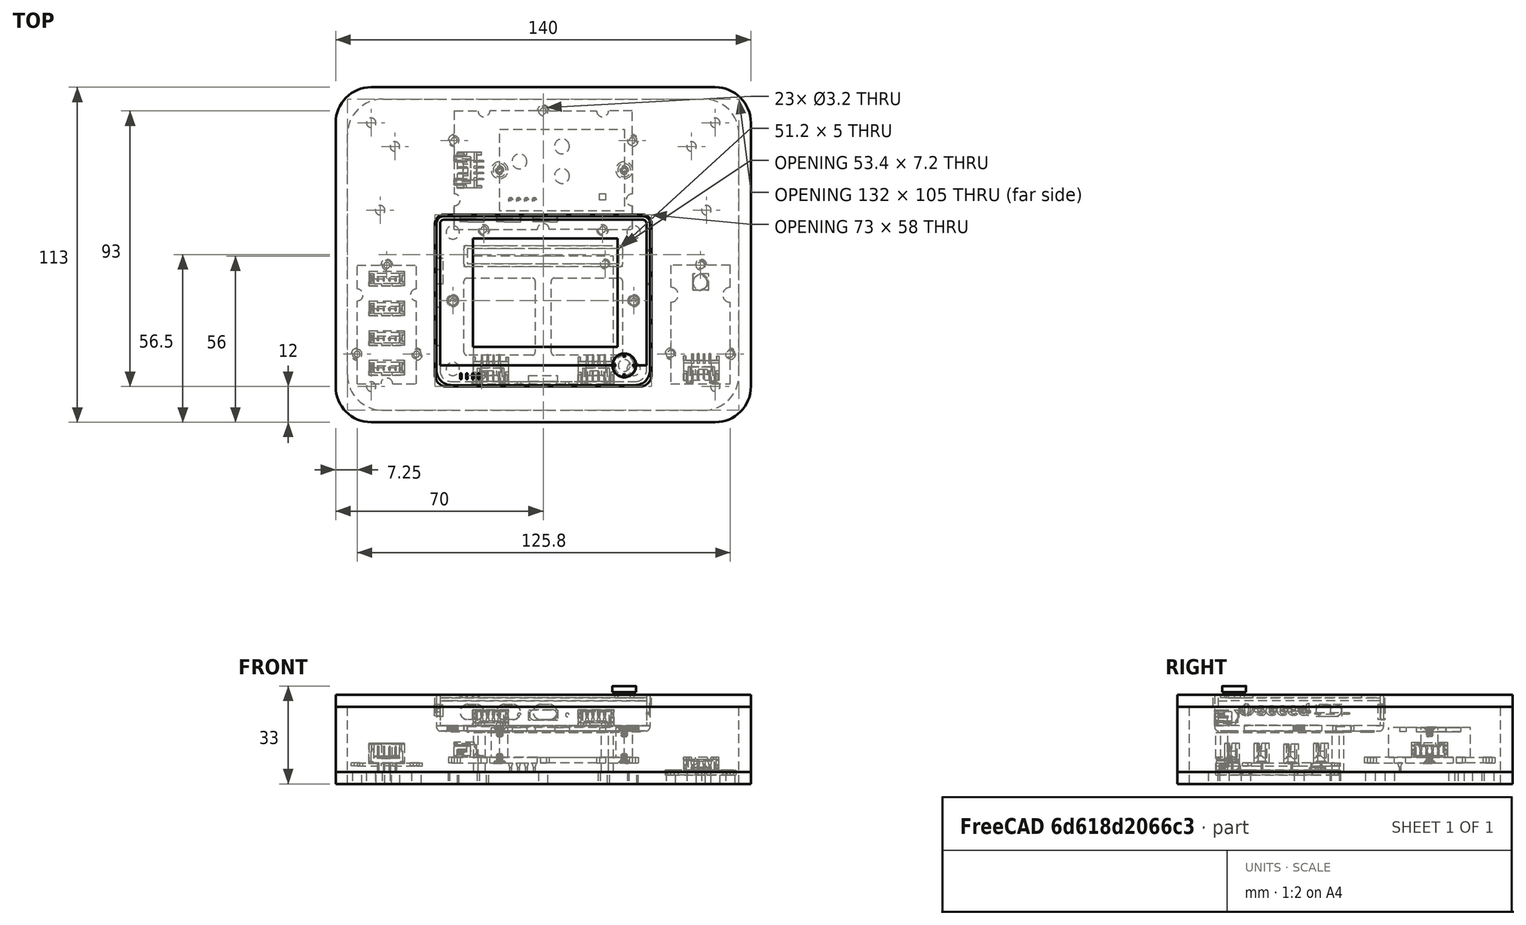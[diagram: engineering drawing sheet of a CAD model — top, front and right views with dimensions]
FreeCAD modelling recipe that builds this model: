
FCSTD DOCUMENT  (FreeCAD 0.20R29177 (Git))
Label: outBuild
License: All rights reserved
LicenseURL: http://en.wikipedia.org/wiki/All_rights_reserved
objects: Part::Cylinder×45, Part::Cut×32, Part::Box×26, Part::MultiFuse×15, Part::Feature×4
note: 122 computed .brp shape members not serialized (recipe doc carries the construction recipe); baked Part::Feature solids carry a one-line shape summary decoded from their .brp

FEATURE [Part::Feature] Feature  label="Grove I2C hub"
  Placement = pos=(15,60,9) rot=(0,0,1;3.14159rad)
  shape: bbox 24 x 42 x 9.849 mm, 365 faces, 5 solids (baked)
FEATURE [Part::Feature] Feature001  label="Grove_BME280"
  Placement = pos=(113,14,3) rot=(0.57735,0.57735,0.57735;2.0944rad)
  shape: bbox 23.8 x 41.9 x 6.016 mm, 221 faces, 2 solids (baked)
FEATURE [Part::Box] Box043  label="ips7100"
  AttacherType = Attacher::AttachEngine3D
  Height = 13.4
  Length = 47.1
  Width = 43.1
FEATURE [Part::Cylinder] Cylinder045  label="Cylinder"
  Angle = 360
  AttacherType = Attacher::AttachEngine3D
  FirstAngle = 0
  Height = 20
  Placement = pos=(2.75,2.75,0) rot=(0,0,1;0rad)
  Radius = 1.2
  SecondAngle = 0
FEATURE [Part::Cylinder] Cylinder046
  Angle = 360
  AttacherType = Attacher::AttachEngine3D
  FirstAngle = 0
  Height = 20
  Placement = pos=(44.35,40.35,0) rot=(0,0,1;0rad)
  Radius = 1.2
  SecondAngle = 0
FEATURE [Part::MultiFuse] Fusion030
  Shapes = -> [Cylinder045,Cylinder046]
FEATURE [Part::Cut] Cut012  label="ips7100s"
  Base = -> Box043
  Placement = pos=(46.5,13,4) rot=(0,0,1;0rad)
  Tool = -> Fusion030
FEATURE [Part::Feature] Feature002  label="Wio Terminal"
  Placement = pos=(70,41,30) rot=(0,0,1;0rad)
  shape: bbox 73.03 x 57.91 x 15.61 mm, 2405 faces, 30 solids (baked)
FEATURE [Part::Feature] Feature003  label="Seed Grove SCD30"
  Placement = pos=(40,65,9) rot=(1,0,0;4.71239rad)
  shape: bbox 64 x 44 x 15.1 mm, 422 faces, 13 solids (baked)
FEATURE [Part::Box] Box  label="base"
  AttacherType = Attacher::AttachEngine3D
  Height = 4
  Length = 140
  Width = 113
FEATURE [Part::Cylinder] Cylinder047  label="Cylinder048"
  Angle = 360
  AttacherType = Attacher::AttachEngine3D
  FirstAngle = 0
  Height = 10
  Placement = pos=(7.25,23,0) rot=(0,0,1;0rad)
  Radius = 1.6
  SecondAngle = 0
FEATURE [Part::Cylinder] Cylinder048  label="Cylinder049"
  Angle = 360
  AttacherType = Attacher::AttachEngine3D
  FirstAngle = 0
  Height = 10
  Placement = pos=(27.25,23,0) rot=(0,0,1;0rad)
  Radius = 1.6
  SecondAngle = 0
FEATURE [Part::Cylinder] Cylinder049  label="Cylinder050"
  Angle = 360
  AttacherType = Attacher::AttachEngine3D
  FirstAngle = 0
  Height = 10
  Placement = pos=(17.25,53,0) rot=(0,0,1;0rad)
  Radius = 1.6
  SecondAngle = 0
FEATURE [Part::MultiFuse] Fusion  label="i2cCuts"
  Shapes = -> [Cylinder047,Cylinder048,Cylinder049]
FEATURE [Part::Cylinder] Cylinder050  label="Cylinder051"
  Angle = 360
  AttacherType = Attacher::AttachEngine3D
  FirstAngle = 0
  Height = 10
  Placement = pos=(7.25,23,0) rot=(0,0,1;0rad)
  Radius = 1.6
  SecondAngle = 0
FEATURE [Part::Cylinder] Cylinder051  label="Cylinder052"
  Angle = 360
  AttacherType = Attacher::AttachEngine3D
  FirstAngle = 0
  Height = 10
  Placement = pos=(27.25,23,0) rot=(0,0,1;0rad)
  Radius = 1.6
  SecondAngle = 0
FEATURE [Part::Cylinder] Cylinder052  label="Cylinder053"
  Angle = 360
  AttacherType = Attacher::AttachEngine3D
  FirstAngle = 0
  Height = 10
  Placement = pos=(17.25,53,0) rot=(0,0,1;0rad)
  Radius = 1.6
  SecondAngle = 0
FEATURE [Part::MultiFuse] Fusion031  label="scdCuts001"
  Placement = pos=(105.8,0,0) rot=(0,0,1;0rad)
  Shapes = -> [Cylinder050,Cylinder051,Cylinder052]
FEATURE [Part::Cylinder] Cylinder053  label="Cylinder054"
  Angle = 360
  AttacherType = Attacher::AttachEngine3D
  FirstAngle = 0
  Height = 20
  Placement = pos=(2.75,2.75,0) rot=(0,0,1;0rad)
  Radius = 1.6
  SecondAngle = 0
FEATURE [Part::Cylinder] Cylinder054  label="Cylinder055"
  Angle = 360
  AttacherType = Attacher::AttachEngine3D
  FirstAngle = 0
  Height = 20
  Placement = pos=(44.35,40.35,0) rot=(0,0,1;0rad)
  Radius = 1.6
  SecondAngle = 0
FEATURE [Part::MultiFuse] Fusion032  label="ipsCuts"
  Placement = pos=(46.5,13,0) rot=(0,0,1;0rad)
  Shapes = -> [Cylinder053,Cylinder054]
FEATURE [Part::Cylinder] Cylinder055  label="Cylinder056"
  Angle = 360
  AttacherType = Attacher::AttachEngine3D
  FirstAngle = 0
  Height = 10
  Placement = pos=(50,65,0) rot=(0,0,1;0rad)
  Radius = 1.6
  SecondAngle = 0
FEATURE [Part::Cylinder] Cylinder056  label="Cylinder057"
  Angle = 360
  AttacherType = Attacher::AttachEngine3D
  FirstAngle = 0
  Height = 10
  Placement = pos=(90,65,0) rot=(0,0,1;0rad)
  Radius = 1.6
  SecondAngle = 0
FEATURE [Part::Cylinder] Cylinder057  label="Cylinder058"
  Angle = 360
  AttacherType = Attacher::AttachEngine3D
  FirstAngle = 0
  Height = 10
  Placement = pos=(100,95,0) rot=(0,0,1;0rad)
  Radius = 1.6
  SecondAngle = 0
FEATURE [Part::Cylinder] Cylinder058  label="Cylinder059"
  Angle = 360
  AttacherType = Attacher::AttachEngine3D
  FirstAngle = 0
  Height = 10
  Placement = pos=(40,95,0) rot=(0,0,1;0rad)
  Radius = 1.6
  SecondAngle = 0
FEATURE [Part::Cylinder] Cylinder059  label="Cylinder060"
  Angle = 360
  AttacherType = Attacher::AttachEngine3D
  FirstAngle = 0
  Height = 10
  Placement = pos=(70,105,0) rot=(0,0,1;0rad)
  Radius = 1.6
  SecondAngle = 0
FEATURE [Part::MultiFuse] Fusion033  label="scdCuts"
  Shapes = -> [Cylinder055,Cylinder056,Cylinder057,Cylinder058,Cylinder059]
FEATURE [Part::Cylinder] Cylinder060  label="Cylinder061"
  Angle = 360
  AttacherType = Attacher::AttachEngine3D
  FirstAngle = 0
  Height = 20
  Placement = pos=(39.5,41,0) rot=(0,0,1;0rad)
  Radius = 1.6
  SecondAngle = 0
FEATURE [Part::Cylinder] Cylinder061  label="Cylinder062"
  Angle = 360
  AttacherType = Attacher::AttachEngine3D
  FirstAngle = 0
  Height = 20
  Placement = pos=(100.5,41,0) rot=(0,0,1;0rad)
  Radius = 1.6
  SecondAngle = 0
FEATURE [Part::MultiFuse] Fusion034  label="wioCuts"
  Shapes = -> [Cylinder060,Cylinder061]
FEATURE [Part::MultiFuse] Fusion035  label="cuts"
  Shapes = -> [Fusion,Fusion031,Fusion032,Fusion033,Fusion034]
FEATURE [Part::Cut] Cut  label="base001"
  Base = -> Box
  Tool = -> Fusion035
FEATURE [Part::Cylinder] Cylinder062  label="Cylinder063"
  Angle = 360
  AttacherType = Attacher::AttachEngine3D
  FirstAngle = 0
  Height = 10
  Placement = pos=(12,12,0) rot=(0,0,1;0rad)
  Radius = 1.6
  SecondAngle = 0
FEATURE [Part::Cylinder] Cylinder063  label="Cylinder064"
  Angle = 360
  AttacherType = Attacher::AttachEngine3D
  FirstAngle = 0
  Height = 10
  Placement = pos=(128,12,0) rot=(0,0,1;0rad)
  Radius = 1.6
  SecondAngle = 0
FEATURE [Part::Cylinder] Cylinder064  label="Cylinder065"
  Angle = 360
  AttacherType = Attacher::AttachEngine3D
  FirstAngle = 0
  Height = 10
  Placement = pos=(12,101,0) rot=(0,0,1;0rad)
  Radius = 1.6
  SecondAngle = 0
FEATURE [Part::Cylinder] Cylinder065  label="Cylinder066"
  Angle = 360
  AttacherType = Attacher::AttachEngine3D
  FirstAngle = 0
  Height = 10
  Placement = pos=(128,101,0) rot=(0,0,1;0rad)
  Radius = 1.6
  SecondAngle = 0
FEATURE [Part::MultiFuse] Fusion036  label="outerCuts"
  Shapes = -> [Cylinder062,Cylinder063,Cylinder064,Cylinder065]
FEATURE [Part::Cut] Cut013  label="base003"
  Base = -> Cut
  Tool = -> Fusion036
FEATURE [Part::Box] Box044  label="base002"
  AttacherType = Attacher::AttachEngine3D
  Height = 4
  Length = 12
  Width = 12
FEATURE [Part::Cylinder] Cylinder  label="Cylinder067"
  Angle = 360
  AttacherType = Attacher::AttachEngine3D
  FirstAngle = 0
  Height = 10
  Placement = pos=(12,12,0) rot=(0,-0.707107,0.707107;0rad)
  Radius = 12
  SecondAngle = 0
FEATURE [Part::Cut] Cut014  label="cutOut"
  Base = -> Box044
  Tool = -> Cylinder
FEATURE [Part::Box] Box045  label="base004"
  AttacherType = Attacher::AttachEngine3D
  Height = 4
  Length = 12
  Width = 12
FEATURE [Part::Cylinder] Cylinder066  label="Cylinder068"
  Angle = 360
  AttacherType = Attacher::AttachEngine3D
  FirstAngle = 0
  Height = 10
  Placement = pos=(12,12,0) rot=(0,-0.707107,0.707107;0rad)
  Radius = 12
  SecondAngle = 0
FEATURE [Part::Cut] Cut015  label="cutOut001"
  Base = -> Box045
  Placement = pos=(140,-5.2e-15,0) rot=(0,0,1;1.5708rad)
  Tool = -> Cylinder066
FEATURE [Part::Box] Box046  label="base005"
  AttacherType = Attacher::AttachEngine3D
  Height = 4
  Length = 12
  Width = 12
FEATURE [Part::Cylinder] Cylinder067  label="Cylinder069"
  Angle = 360
  AttacherType = Attacher::AttachEngine3D
  FirstAngle = 0
  Height = 10
  Placement = pos=(12,12,0) rot=(0,-0.707107,0.707107;0rad)
  Radius = 12
  SecondAngle = 0
FEATURE [Part::Cut] Cut016  label="cutOut002"
  Base = -> Box046
  Placement = pos=(140,113,0) rot=(0,0,1;3.14159rad)
  Tool = -> Cylinder067
FEATURE [Part::Box] Box047  label="base006"
  AttacherType = Attacher::AttachEngine3D
  Height = 4
  Length = 12
  Width = 12
FEATURE [Part::Cylinder] Cylinder068  label="Cylinder070"
  Angle = 360
  AttacherType = Attacher::AttachEngine3D
  FirstAngle = 0
  Height = 10
  Placement = pos=(12,12,0) rot=(0,-0.707107,0.707107;0rad)
  Radius = 12
  SecondAngle = 0
FEATURE [Part::Cut] Cut017  label="cutOut003"
  Base = -> Box047
  Placement = pos=(0,113,0) rot=(0,0,1;4.71239rad)
  Tool = -> Cylinder068
FEATURE [Part::MultiFuse] Fusion037  label="cutOut004"
  Shapes = -> [Cut014,Cut015,Cut016,Cut017]
FEATURE [Part::Cut] Cut018
  Base = -> Cut013
  Tool = -> Fusion037
FEATURE [Part::Cylinder] Cylinder069  label="Cylinder071"
  Angle = 360
  AttacherType = Attacher::AttachEngine3D
  FirstAngle = 0
  Height = 10
  Placement = pos=(15,71.5,0) rot=(0,0,1;0rad)
  Radius = 1.6
  SecondAngle = 0
FEATURE [Part::Cylinder] Cylinder070  label="Cylinder072"
  Angle = 360
  AttacherType = Attacher::AttachEngine3D
  FirstAngle = 0
  Height = 10
  Placement = pos=(125,71.5,0) rot=(0,0,1;0rad)
  Radius = 1.6
  SecondAngle = 0
FEATURE [Part::MultiFuse] Fusion038  label="cuts001"
  Shapes = -> [Cylinder069,Cylinder070]
FEATURE [Part::Cut] Cut019  label="base007"
  Base = -> Cut018
  Tool = -> Fusion038
FEATURE [Part::Cylinder] Cylinder071  label="Cylinder073"
  Angle = 360
  AttacherType = Attacher::AttachEngine3D
  FirstAngle = 0
  Height = 10
  Placement = pos=(20,93,0) rot=(0,0,1;0rad)
  Radius = 1.6
  SecondAngle = 0
FEATURE [Part::Cylinder] Cylinder072  label="Cylinder074"
  Angle = 360
  AttacherType = Attacher::AttachEngine3D
  FirstAngle = 0
  Height = 10
  Placement = pos=(120,93,0) rot=(0,0,1;0rad)
  Radius = 1.6
  SecondAngle = 0
FEATURE [Part::MultiFuse] Fusion039  label="wallMounts"
  Shapes = -> [Cylinder071,Cylinder072]
FEATURE [Part::Cut] Cut020  label="base008"
  Base = -> Cut019
  Tool = -> Fusion039
FEATURE [Part::Box] Box048  label="top"
  AttacherType = Attacher::AttachEngine3D
  Height = 4
  Length = 140
  Width = 113
FEATURE [Part::Box] Box049  label="base009"
  AttacherType = Attacher::AttachEngine3D
  Height = 4
  Length = 12
  Width = 12
FEATURE [Part::Box] Box050  label="base010"
  AttacherType = Attacher::AttachEngine3D
  Height = 4
  Length = 12
  Width = 12
FEATURE [Part::Box] Box051  label="base011"
  AttacherType = Attacher::AttachEngine3D
  Height = 4
  Length = 12
  Width = 12
FEATURE [Part::Box] Box052  label="base012"
  AttacherType = Attacher::AttachEngine3D
  Height = 4
  Length = 12
  Width = 12
FEATURE [Part::Cylinder] Cylinder073  label="Cylinder075"
  Angle = 360
  AttacherType = Attacher::AttachEngine3D
  FirstAngle = 0
  Height = 10
  Placement = pos=(12,12,0) rot=(0,-0.707107,0.707107;0rad)
  Radius = 12
  SecondAngle = 0
FEATURE [Part::Cut] Cut021  label="cutOut005"
  Base = -> Box049
  Tool = -> Cylinder073
FEATURE [Part::Cylinder] Cylinder074  label="Cylinder076"
  Angle = 360
  AttacherType = Attacher::AttachEngine3D
  FirstAngle = 0
  Height = 10
  Placement = pos=(12,12,0) rot=(0,-0.707107,0.707107;0rad)
  Radius = 12
  SecondAngle = 0
FEATURE [Part::Cut] Cut022  label="cutOut006"
  Base = -> Box050
  Placement = pos=(140,-5.2e-15,0) rot=(0,0,1;1.5708rad)
  Tool = -> Cylinder074
FEATURE [Part::Cylinder] Cylinder075  label="Cylinder077"
  Angle = 360
  AttacherType = Attacher::AttachEngine3D
  FirstAngle = 0
  Height = 10
  Placement = pos=(12,12,0) rot=(0,-0.707107,0.707107;0rad)
  Radius = 12
  SecondAngle = 0
FEATURE [Part::Cut] Cut023  label="cutOut007"
  Base = -> Box051
  Placement = pos=(140,113,0) rot=(0,0,1;3.14159rad)
  Tool = -> Cylinder075
FEATURE [Part::Cylinder] Cylinder076  label="Cylinder078"
  Angle = 360
  AttacherType = Attacher::AttachEngine3D
  FirstAngle = 0
  Height = 10
  Placement = pos=(12,12,0) rot=(0,-0.707107,0.707107;0rad)
  Radius = 12
  SecondAngle = 0
FEATURE [Part::Cut] Cut024  label="cutOut008"
  Base = -> Box052
  Placement = pos=(0,113,0) rot=(0,0,-1;1.5708rad)
  Tool = -> Cylinder076
FEATURE [Part::MultiFuse] Fusion040  label="cutOut009"
  Shapes = -> [Cut021,Cut022,Cut023,Cut024]
FEATURE [Part::Cut] Cut025  label="top001"
  Base = -> Box048
  Placement = pos=(0,0,26) rot=(0,0,1;0rad)
  Tool = -> Fusion040
FEATURE [Part::Box] Box053  label="Cube"
  AttacherType = Attacher::AttachEngine3D
  Height = 10
  Length = 73
  Placement = pos=(33.5,12,26) rot=(0,0,1;0rad)
  Width = 58
FEATURE [Part::Box] Box054  label="Cube001"
  AttacherType = Attacher::AttachEngine3D
  Height = 10
  Length = 3
  Placement = pos=(33.5,67,26) rot=(0,0,1;0rad)
  Width = 3
FEATURE [Part::Cylinder] Cylinder077  label="Cylinder079"
  Angle = 360
  AttacherType = Attacher::AttachEngine3D
  FirstAngle = 0
  Height = 10
  Placement = pos=(36.5,67,26) rot=(0,0,1;0rad)
  Radius = 3
  SecondAngle = 0
FEATURE [Part::Cut] Cut026  label="outCutsDisplay"
  Base = -> Box054
  Tool = -> Cylinder077
FEATURE [Part::Box] Box055  label="Cube002"
  AttacherType = Attacher::AttachEngine3D
  Height = 10
  Length = 3
  Placement = pos=(33.5,67,26) rot=(0,0,1;0rad)
  Width = 3
FEATURE [Part::Cylinder] Cylinder078  label="Cylinder080"
  Angle = 360
  AttacherType = Attacher::AttachEngine3D
  FirstAngle = 0
  Height = 10
  Placement = pos=(36.5,67,26) rot=(0,0,1;0rad)
  Radius = 3
  SecondAngle = 0
FEATURE [Part::Cut] Cut027  label="outCutsDisplay001"
  Base = -> Box055
  Placement = pos=(36.5,103.5,0) rot=(0,0,1;4.71239rad)
  Tool = -> Cylinder078
FEATURE [Part::Box] Box057  label="Cube004"
  AttacherType = Attacher::AttachEngine3D
  Height = 10
  Length = 4
  Placement = pos=(32.5,67,26) rot=(0,0,1;0rad)
  Width = 4
FEATURE [Part::Cylinder] Cylinder080  label="Cylinder082"
  Angle = 360
  AttacherType = Attacher::AttachEngine3D
  FirstAngle = 0
  Height = 10
  Placement = pos=(36.5,67,26) rot=(0,0,1;0rad)
  Radius = 4
  SecondAngle = 0
FEATURE [Part::Cut] Cut029  label="outCutsDisplay003"
  Base = -> Box057
  Placement = pos=(104.5,-20.5,0) rot=(0,0,1;1.5708rad)
  Tool = -> Cylinder080
FEATURE [Part::Box] Box058  label="Cube005"
  AttacherType = Attacher::AttachEngine3D
  Height = 10
  Length = 4
  Placement = pos=(32.5,67,26) rot=(0,0,1;0rad)
  Width = 4
FEATURE [Part::Cylinder] Cylinder081  label="Cylinder083"
  Angle = 360
  AttacherType = Attacher::AttachEngine3D
  FirstAngle = 0
  Height = 10
  Placement = pos=(36.5,67,26) rot=(0,0,1;0rad)
  Radius = 4
  SecondAngle = 0
FEATURE [Part::Cut] Cut030  label="outCutsDisplay004"
  Base = -> Box058
  Placement = pos=(139,83,0) rot=(0,0,1;3.14159rad)
  Tool = -> Cylinder081
FEATURE [Part::MultiFuse] Fusion041  label="displayCuts"
  Shapes = -> [Cut029,Cut030,Cut026,Cut027]
FEATURE [Part::Cut] Cut031  label="topCut"
  Base = -> Box053
  Tool = -> Fusion041
FEATURE [Part::Cut] Cut032  label="top002"
  Base = -> Cut025
  Tool = -> Cut031
FEATURE [Part::Box] Box059  label="base013"
  AttacherType = Attacher::AttachEngine3D
  Height = 26
  Length = 140
  Width = 113
FEATURE [Part::Box] Box060  label="base014"
  AttacherType = Attacher::AttachEngine3D
  Height = 26
  Length = 12
  Width = 12
FEATURE [Part::Box] Box061  label="base015"
  AttacherType = Attacher::AttachEngine3D
  Height = 26
  Length = 12
  Width = 12
FEATURE [Part::Box] Box062  label="base016"
  AttacherType = Attacher::AttachEngine3D
  Height = 26
  Length = 12
  Width = 12
FEATURE [Part::Box] Box063  label="base017"
  AttacherType = Attacher::AttachEngine3D
  Height = 26
  Length = 12
  Width = 12
FEATURE [Part::Cylinder] Cylinder082  label="Cylinder084"
  Angle = 360
  AttacherType = Attacher::AttachEngine3D
  FirstAngle = 0
  Height = 26
  Placement = pos=(12,12,0) rot=(0,-0.707107,0.707107;0rad)
  Radius = 12
  SecondAngle = 0
FEATURE [Part::Cut] Cut033  label="cutOut010"
  Base = -> Box060
  Tool = -> Cylinder082
FEATURE [Part::Cylinder] Cylinder083  label="Cylinder085"
  Angle = 360
  AttacherType = Attacher::AttachEngine3D
  FirstAngle = 0
  Height = 26
  Placement = pos=(12,12,0) rot=(0,-0.707107,0.707107;0rad)
  Radius = 12
  SecondAngle = 0
FEATURE [Part::Cut] Cut034  label="cutOut011"
  Base = -> Box061
  Placement = pos=(140,-5.2e-15,0) rot=(0,0,1;1.5708rad)
  Tool = -> Cylinder083
FEATURE [Part::Cylinder] Cylinder084  label="Cylinder086"
  Angle = 360
  AttacherType = Attacher::AttachEngine3D
  FirstAngle = 0
  Height = 26
  Placement = pos=(12,12,0) rot=(0,-0.707107,0.707107;0rad)
  Radius = 12
  SecondAngle = 0
FEATURE [Part::Cut] Cut035  label="cutOut012"
  Base = -> Box062
  Placement = pos=(140,113,0) rot=(0,0,1;3.14159rad)
  Tool = -> Cylinder084
FEATURE [Part::Cylinder] Cylinder085  label="Cylinder087"
  Angle = 360
  AttacherType = Attacher::AttachEngine3D
  FirstAngle = 0
  Height = 26
  Placement = pos=(12,12,0) rot=(0,-0.707107,0.707107;0rad)
  Radius = 12
  SecondAngle = 0
FEATURE [Part::Cut] Cut036  label="cutOut013"
  Base = -> Box063
  Placement = pos=(0,113,0) rot=(0,0,-1;1.5708rad)
  Tool = -> Cylinder085
FEATURE [Part::MultiFuse] Fusion042  label="cuts002"
  Shapes = -> [Cut036,Cut033,Cut034,Cut035]
FEATURE [Part::Cut] Cut037  label="wall"
  Base = -> Box059
  Tool = -> Fusion042
FEATURE [Part::Box] Box064  label="base018"
  AttacherType = Attacher::AttachEngine3D
  Height = 26
  Length = 132
  Placement = pos=(4,4,0) rot=(0,0,1;0rad)
  Width = 105
FEATURE [Part::Box] Box065  label="base019"
  AttacherType = Attacher::AttachEngine3D
  Height = 26
  Length = 12
  Width = 12
FEATURE [Part::Box] Box066  label="base020"
  AttacherType = Attacher::AttachEngine3D
  Height = 26
  Length = 12
  Width = 12
FEATURE [Part::Box] Box067  label="base021"
  AttacherType = Attacher::AttachEngine3D
  Height = 26
  Length = 12
  Width = 12
FEATURE [Part::Box] Box068  label="base022"
  AttacherType = Attacher::AttachEngine3D
  Height = 26
  Length = 12
  Width = 12
FEATURE [Part::Cylinder] Cylinder086  label="Cylinder088"
  Angle = 360
  AttacherType = Attacher::AttachEngine3D
  FirstAngle = 0
  Height = 26
  Placement = pos=(12,12,0) rot=(0,-0.707107,0.707107;0rad)
  Radius = 12
  SecondAngle = 0
FEATURE [Part::Cut] Cut038  label="cutOut014"
  Base = -> Box065
  Placement = pos=(4,4,0) rot=(0,0,1;0rad)
  Tool = -> Cylinder086
FEATURE [Part::Cylinder] Cylinder087  label="Cylinder089"
  Angle = 360
  AttacherType = Attacher::AttachEngine3D
  FirstAngle = 0
  Height = 26
  Placement = pos=(12,12,0) rot=(0,-0.707107,0.707107;0rad)
  Radius = 12
  SecondAngle = 0
FEATURE [Part::Cut] Cut039  label="cutOut015"
  Base = -> Box066
  Placement = pos=(136,4,0) rot=(0,0,1;1.5708rad)
  Tool = -> Cylinder087
FEATURE [Part::Cylinder] Cylinder088  label="Cylinder090"
  Angle = 360
  AttacherType = Attacher::AttachEngine3D
  FirstAngle = 0
  Height = 26
  Placement = pos=(12,12,0) rot=(0,-0.707107,0.707107;0rad)
  Radius = 12
  SecondAngle = 0
FEATURE [Part::Cut] Cut040  label="cutOut016"
  Base = -> Box067
  Placement = pos=(136,109,0) rot=(0,0,1;3.14159rad)
  Tool = -> Cylinder088
FEATURE [Part::Cylinder] Cylinder089  label="Cylinder091"
  Angle = 360
  AttacherType = Attacher::AttachEngine3D
  FirstAngle = 0
  Height = 26
  Placement = pos=(12,12,0) rot=(0,-0.707107,0.707107;0rad)
  Radius = 12
  SecondAngle = 0
FEATURE [Part::Cut] Cut041  label="cutOut017"
  Base = -> Box068
  Placement = pos=(4,109,0) rot=(0,0,-1;1.5708rad)
  Tool = -> Cylinder089
FEATURE [Part::MultiFuse] Fusion043  label="cuts003"
  Shapes = -> [Cut041,Cut038,Cut039,Cut040]
FEATURE [Part::Cut] Cut042  label="wallCut"
  Base = -> Box064
  Tool = -> Fusion043
FEATURE [Part::Cut] Cut043  label="wall001"
  Base = -> Cut037
  Tool = -> Cut042
